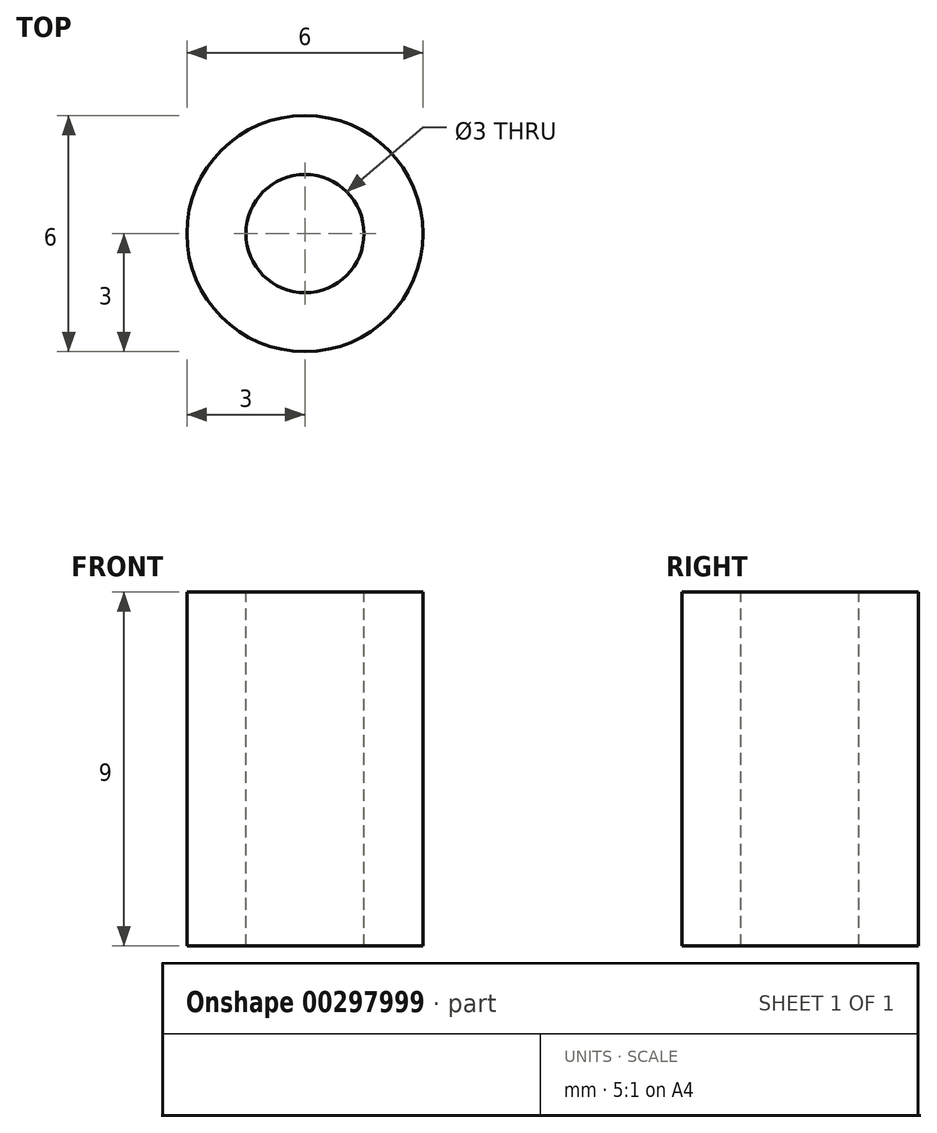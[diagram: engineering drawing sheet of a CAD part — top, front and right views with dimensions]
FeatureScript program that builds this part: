
annotation { "Feature Type Name" : "Feature", "Feature Type Description" : "" }
export const myFeature = defineFeature(function(context is Context, id is Id, definition is map)
    precondition{}
    {
        {
            var Q0;
            Q0=qCreatedBy(makeId("Top.planeOp"),FACE);
            var sketch = newSketch(context, id + "F0", { "sketchPlane" : qUnion([Q0])});
            skCircle(sketch, "E0", {"center": v(0, 0) * mm, "radius": 3 * mm});
            skSolve(sketch);
        }
        {
            var Q0;
            Q0=makeQuery(id+"F0.imprint","IMPRINT",FACE,{"disambiguationData":[TD([[makeQuery(id+"F0.imprint","IMPRINT",EDGE,{"derivedFrom":sQuery(id+"F0.wireOp",EDGE,"E0")}),1.0]])]});
            extrude(context, id + "F1", {"entities" : qUnion([Q0]), "oppositeDirection" : true, "depth" : 5 * mm});
        }
        {
            var Q0;
            Q0=qCreatedBy(makeId("Top.planeOp"),FACE);
            var sketch = newSketch(context, id + "F2", { "sketchPlane" : qUnion([Q0])});
            skCircle(sketch, "E1", {"center": v(0, 0) * mm, "radius": 3 * mm});
            skSolve(sketch);
        }
        {
            var Q0;
            Q0=makeQuery(id+"F2.imprint","IMPRINT",FACE,{"disambiguationData":[TD([[makeQuery(id+"F2.imprint","IMPRINT",EDGE,{"derivedFrom":sQuery(id+"F2.wireOp",EDGE,"E1")}),1.0]])]});
            extrude(context, id + "F3", {"entities" : qUnion([Q0]), "operationType" : NewBodyOperationType.ADD, "depth" : 4 * mm});
        }
        {
            var Q0;
            Q0=makeQuery(id+"F3.opExtrude","CAP_FACE",FACE,{"disambiguationData":[OSD([sQuery(id+"F2.wireOp",EDGE,"E1")])],"isStart":false});
            var sketch = newSketch(context, id + "F4", { "sketchPlane" : qUnion([Q0])});
            skPoint(sketch, "E2", {"position": v(0, 0) * mm});
            skSolve(sketch);
        }
        {
            var Q0;
            Q0=sQuery(id+"F4.wireOp",VERTEX,"E2");
            var Q1;
            Q1=makeQuery(id+"F1.opExtrude","SWEPT_BODY",BODY,{"disambiguationData":[OSD([sQuery(id+"F0.wireOp",EDGE,"E0")])]});
            hole(context, id + "F5", {"style" : HoleStyle.SIMPLE, "endStyle" : HoleEndStyle.BLIND, "holeDiameter" : 3 * mm, "holeDepth" : 15 * mm, "tappedDepth" : 12 * mm, "tapClearance" : 3, "locations" : qUnion([Q0]), "scope" : qUnion([Q1])});
        }
    });
